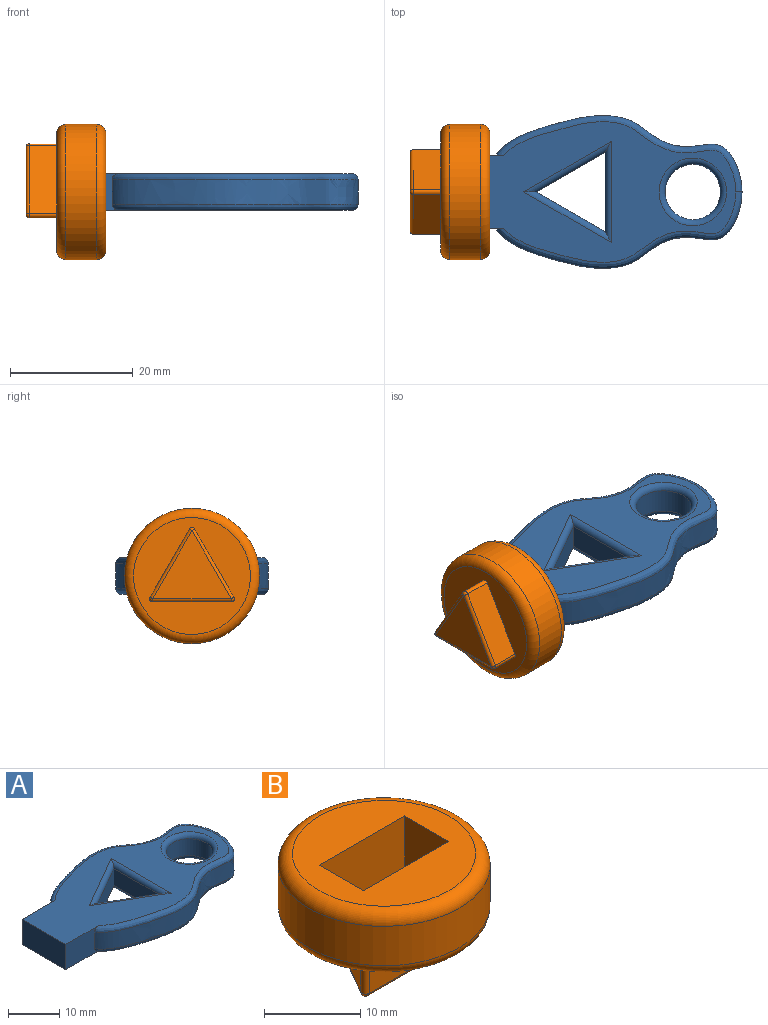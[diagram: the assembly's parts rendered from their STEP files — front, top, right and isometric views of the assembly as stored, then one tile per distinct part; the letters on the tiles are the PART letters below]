
ASSEMBLY  parts=2 mates=1
PART A: 23 faces, bbox 48.4x25.2x6.4 mm
  f0: plane 12x6mm, normal (-1,0,0), area 72mm2, adj f1,f8,f9,f10
  f1: plane 9.62x6.37mm, normal (0,-1,0), area 48.5mm2, adj f0,f2,f9,f10,f11,f17
  f2: extruded ~40x12.43mm, area 192.2mm2, adj f1,f3,f11,f17
  f3: extruded ~40x12.43mm, area 192.2mm2, adj f2,f8,f12,f18
  f4: plane 13x4mm, normal (-1,0,0), area 52mm2, adj f5,f7,f15,f21
  f5: plane 11.26x6.5mm, normal (0.5,0.87,0), area 52mm2, adj f4,f7,f14,f20
  f6: cylinder r=4.5mm len=9mm, axis (0,0,-1), area 113.1mm2, adj f13,f19
  f7: plane 11.26x6.5mm, normal (0.5,-0.87,0), area 52mm2, adj f4,f5,f16,f22
  f8: plane 9.62x6.37mm, normal (0,1,0), area 48.5mm2, adj f0,f3,f9,f10,f12,f18
  f9: plane 47x22.86mm, normal (0,0,1), area 547.2mm2, adj f0,f1,f8,f17,f18,f19,f20,f21
  f10: plane 47x22.86mm, normal (0,0,-1), area 547.2mm2, adj f0,f1,f8,f11,f12,f13,f14,f15
  f11: bspline ~40.69x12.66mm, area 73.4mm2, adj f1,f2,f10,f12
  f12: bspline ~40.69x12.66mm, area 73.4mm2, adj f3,f8,f10,f11
  f13: torus R=5.5mm, axis (0,0,1), area 48mm2, adj f6,f10
  f14: cylinder r=1mm len=14.76mm, axis (-0.87,0.5,0), area 23.1mm2, adj f5,f10,f15,f16
  f15: cylinder r=1mm len=16.46mm, axis (0,-1,0), area 23.1mm2, adj f4,f10,f14,f16
  f16: cylinder r=1mm len=14.76mm, axis (0.87,0.5,0), area 23.1mm2, adj f7,f10,f14,f15
  f17: bspline ~40.69x12.66mm, area 73.4mm2, adj f1,f2,f9,f18
  f18: bspline ~40.69x12.66mm, area 73.4mm2, adj f3,f8,f9,f17
  f19: torus R=5.5mm, axis (0,0,1), area 48mm2, adj f6,f9
  f20: cylinder r=1mm len=14.76mm, axis (0.87,-0.5,0), area 23.1mm2, adj f5,f9,f21,f22
  f21: cylinder r=1mm len=16.46mm, axis (0,1,0), area 23.1mm2, adj f4,f9,f20,f22
  f22: cylinder r=1mm len=14.76mm, axis (-0.87,-0.5,0), area 23.1mm2, adj f7,f9,f20,f21
PART B: 23 faces, bbox 23.8x23.8x13 mm
  f0: plane 19x19mm, normal (0,0,1), area 202.3mm2, adj f3,f4,f5,f6,f9
  f1: cylinder r=11mm len=22mm, axis (0,0,-1), area 345.6mm2, adj f8,f9
  f2: plane 19x19mm, normal (0,0,-1), area 193mm2, adj f8,f10,f11,f12,f14,f16,f22
  f3: plane 7x6.5mm, normal (-1,0,0), area 45.5mm2, adj f0,f4,f6,f7
  f4: plane 12.5x7mm, normal (0,-1,0), area 87.5mm2, adj f0,f3,f5,f7
  f5: plane 7x6.5mm, normal (1,0,0), area 45.5mm2, adj f0,f4,f6,f7
  f6: plane 12.5x7mm, normal (0,1,0), area 87.5mm2, adj f0,f3,f5,f7
  f7: plane 12.5x6.5mm, normal (0,0,1), area 81.2mm2, adj f3,f4,f5,f6
  f8: torus R=9.5mm, axis (0,0,1), area 154.8mm2, adj f1,f2
  f9: torus R=9.5mm, axis (0,0,1), area 154.8mm2, adj f0,f1
  f10: plane 11.06x6.38mm, normal (0.87,0.5,0), area 57.5mm2, adj f2,f16,f20,f22
  f11: plane 11.06x6.38mm, normal (-0.87,0.5,0), area 57.5mm2, adj f2,f14,f19,f22
  f12: plane 12.77x4.5mm, normal (0,-1,0), area 57.5mm2, adj f2,f14,f15,f16
  f13: plane 12.77x11.06mm, normal (0,0,-1), area 70.6mm2, adj f15,f19,f20
  f14: cylinder r=0.5mm len=4.5mm, axis (0,0,1), area 4.7mm2, adj f2,f11,f12,f17
  f15: cylinder r=0.5mm len=12.77mm, axis (-1,0,0), area 10mm2, adj f12,f13,f17,f18
  f16: cylinder r=0.5mm len=4.5mm, axis (0,0,1), area 4.7mm2, adj f2,f10,f12,f18
  f17: sphere r=0.5mm, area 0.5mm2, adj f14,f15,f19
  f18: sphere r=0.5mm, area 0.5mm2, adj f15,f16,f20
  f19: cylinder r=0.5mm len=11.31mm, axis (0.5,0.87,0), area 10mm2, adj f11,f13,f17,f21
  f20: cylinder r=0.5mm len=11.31mm, axis (0.5,-0.87,0), area 10mm2, adj f10,f13,f18,f21
  f21: sphere r=0.5mm, area 0.5mm2, adj f19,f20,f22
  f22: cylinder r=0.5mm len=4.5mm, axis (0,0,1), area 4.7mm2, adj f2,f10,f11,f21
PLACE A t=(-1.79,8.56,-9.87)mm fixed
PLACE B rot(axis=(0.58,0.58,0.58),120deg) t=(-2.79,8.56,-6.87)mm
MATE fastened A.f0 <-> B.f1  axis (-1,0,0) through (-1.79,8.56,-6.87)mm
